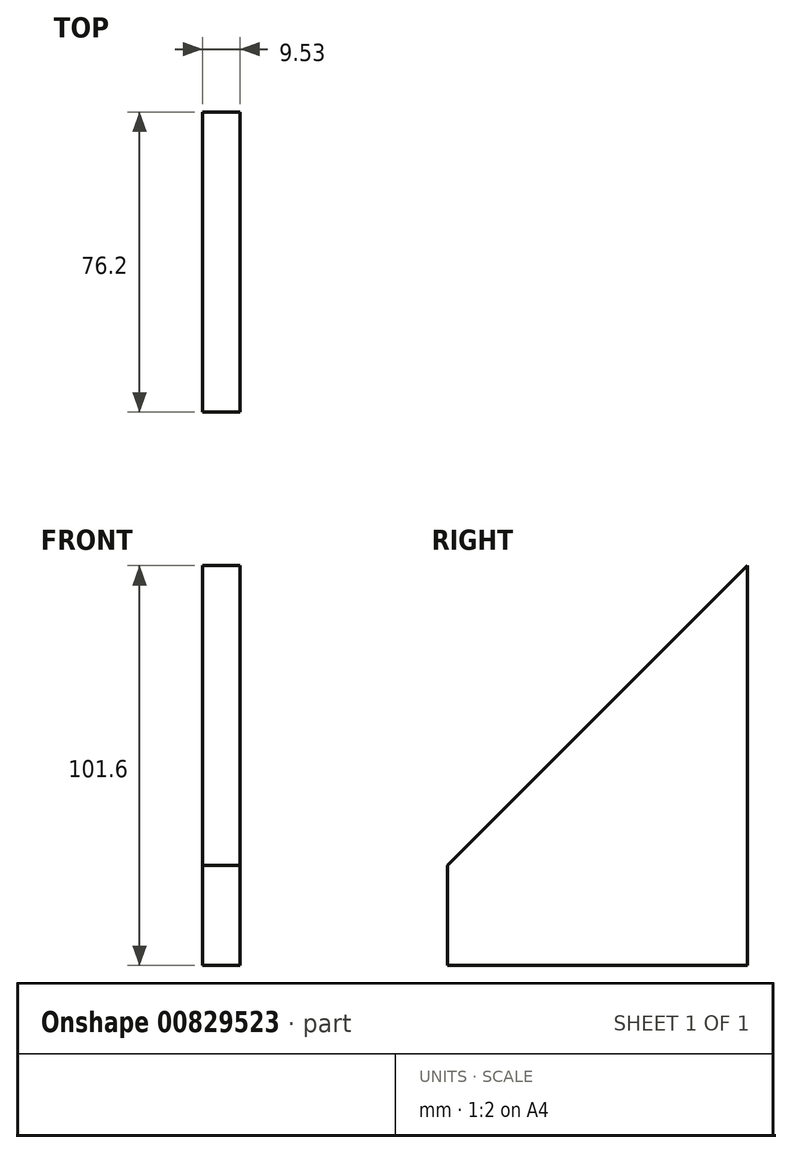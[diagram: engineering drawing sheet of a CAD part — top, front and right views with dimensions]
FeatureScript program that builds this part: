
annotation { "Feature Type Name" : "Feature", "Feature Type Description" : "" }
export const myFeature = defineFeature(function(context is Context, id is Id, definition is map)
    precondition{}
    {
        {
            var Q0;
            Q0=qCreatedBy(makeId("Right.planeOp"),FACE);
            var sketch = newSketch(context, id + "F0", { "sketchPlane" : qUnion([Q0])});
            skLineSegment(sketch, "E0", {"start": v(0, 0) * mm, "end": v(0, 101.6) * mm});
            skLineSegment(sketch, "E1", {"start": v(0, 101.6) * mm, "end": v(-76.2, 25.4) * mm});
            skLineSegment(sketch, "E2", {"start": v(-76.2, 25.4) * mm, "end": v(-76.2, 0) * mm});
            skLineSegment(sketch, "E3", {"start": v(-76.2, 0) * mm, "end": v(0, 0) * mm});
            skSolve(sketch);
        }
        {
            var Q0;
            Q0 = qSketchRegion(id + "F0", true);
            extrude(context, id + "F1", {"entities" : qUnion([Q0]), "depth" : 9.52 * mm, "offsetDistance" : 25.4 * mm});
        }
    });
